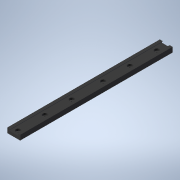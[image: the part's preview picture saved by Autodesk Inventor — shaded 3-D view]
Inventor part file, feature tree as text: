
AUTODESK INVENTOR PART (.ipt)
format: ipt  version: 2021 (Build 250183000, 183)  size: 140,800 bytes
history: native  units: mm
features: extrude x3, sketch x3, projected_geometry x2
ambient origin geometry x8: Origin, YZ Plane, XZ Plane, XY Plane, X Axis, Y Axis, Z Axis, Center Point
bodies: Solid1 (feature_tree)
feature tree (8):
  extrude  "Extrusion1"  Depth=3.5mm
  extrude  "Extrusion2"  Depth=170.0mm TaperAngle=0.0deg
  extrude  "Extrusion3"  Depth=5.5mm
  sketch  "Sketch1"  dims[d0=14.0mm d2=3.5mm]
  sketch  "Sketch2"  dims[d4=10.0mm d5=170.0mm d6=0.0mm]
  sketch  "Sketch3"  dims[d7=3.2mm d8=15.0mm d9=20.0mm d10=30.0mm d11=30.0mm d12=30.0mm d13=30.0mm d14=0.0mm d15=0.0mm d16=6.0mm d17=2.5mm d18=0.0mm d19=5.5mm d20=8.0mm]
  projected_geometry  "Projected Loop1"
  projected_geometry  "Projected Loop2"
